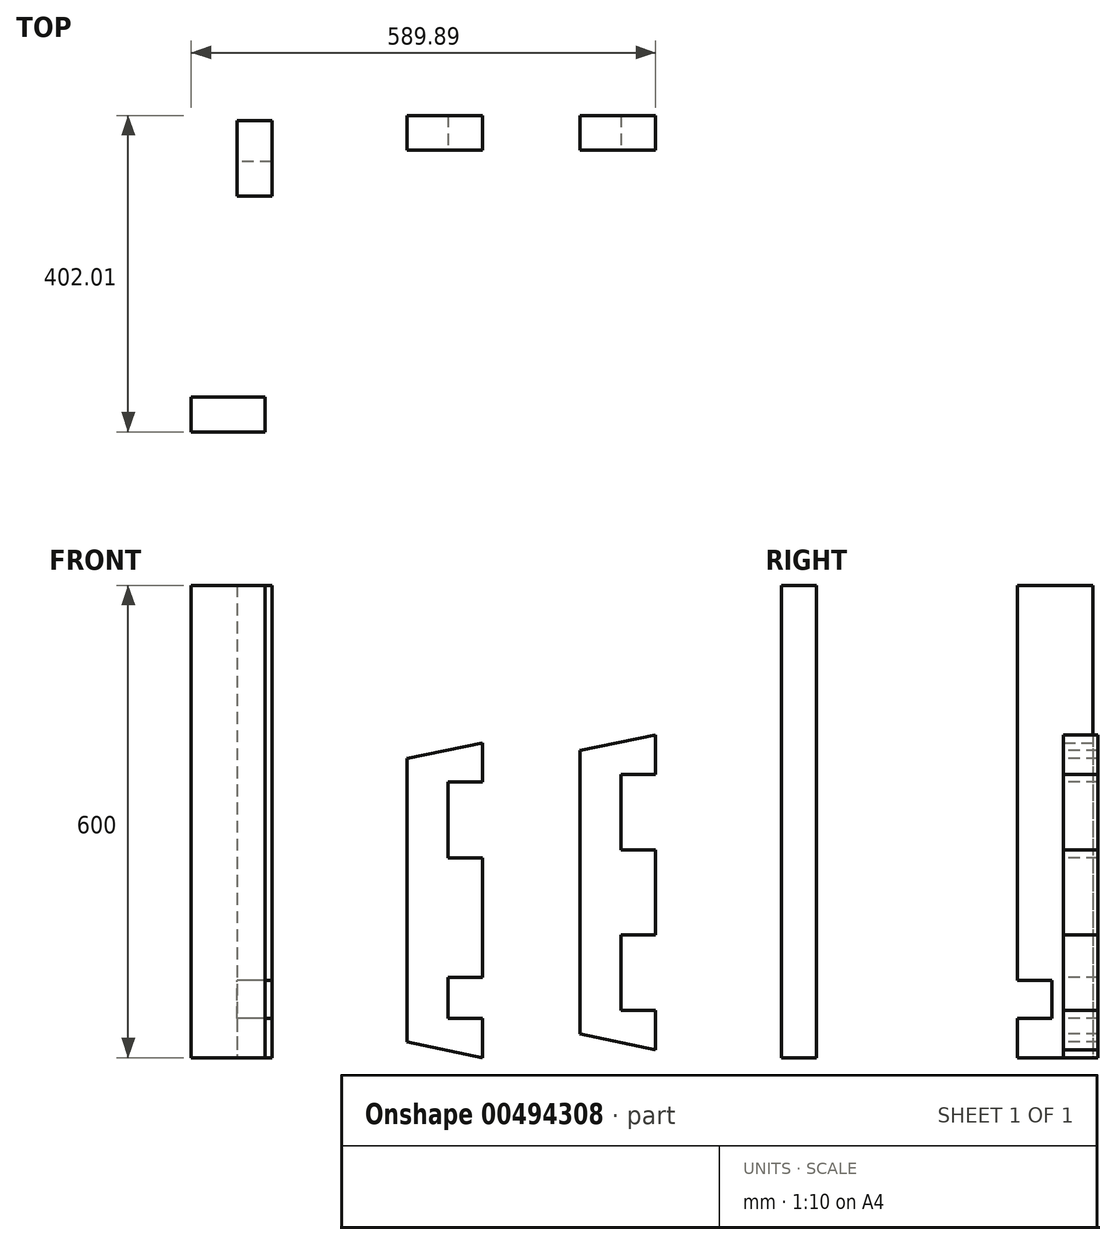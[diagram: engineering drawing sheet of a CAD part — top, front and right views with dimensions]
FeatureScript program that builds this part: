
annotation { "Feature Type Name" : "Feature", "Feature Type Description" : "" }
export const myFeature = defineFeature(function(context is Context, id is Id, definition is map)
    precondition{}
    {
        {
            var Q0;
            Q0=qCreatedBy(makeId("Top.planeOp"),FACE);
            var sketch = newSketch(context, id + "F0", { "sketchPlane" : qUnion([Q0])});
            skLineSegment(sketch, "E0.bottom", {"start": v(0, 0) * mm, "end": v(-96, 0) * mm});
            skLineSegment(sketch, "E0.top", {"start": v(0, 44) * mm, "end": v(-96, 44) * mm});
            skLineSegment(sketch, "E0.left", {"start": v(0, 0) * mm, "end": v(0, 44) * mm});
            skLineSegment(sketch, "E0.right", {"start": v(-96, 0) * mm, "end": v(-96, 44) * mm});
            skSolve(sketch);
        }
        {
            var Q0;
            Q0 = qSketchRegion(id + "F0", true);
            extrude(context, id + "F1", {"entities" : qUnion([Q0]), "depth" : 400 * mm, "offsetDistance" : 25 * mm});
        }
        {
            var Q0;
            Q0=makeQuery(id+"F1.opExtrude","SWEPT_FACE",FACE,{"disambiguationData":[OSD([sQuery(id+"F0.wireOp",EDGE,"E0.bottom")])]});
            var sketch = newSketch(context, id + "F2", { "sketchPlane" : qUnion([Q0])});
            skLineSegment(sketch, "E1.bottom", {"start": v(0, 350) * mm, "end": v(-44, 350) * mm});
            skLineSegment(sketch, "E1.top", {"start": v(0, 254) * mm, "end": v(-44, 254) * mm});
            skLineSegment(sketch, "E1.left", {"start": v(0, 350) * mm, "end": v(0, 254) * mm});
            skLineSegment(sketch, "E1.right", {"start": v(-44, 350) * mm, "end": v(-44, 254) * mm});
            skLineSegment(sketch, "E2.bottom", {"start": v(0, 50) * mm, "end": v(-44, 50) * mm});
            skLineSegment(sketch, "E2.top", {"start": v(0, 102) * mm, "end": v(-44, 102) * mm});
            skLineSegment(sketch, "E2.left", {"start": v(0, 50) * mm, "end": v(0, 102) * mm});
            skLineSegment(sketch, "E2.right", {"start": v(-44, 50) * mm, "end": v(-44, 102) * mm});
            skLineSegment(sketch, "E3", {"start": v(0, 400) * mm, "end": v(-96, 380) * mm});
            skLineSegment(sketch, "E4", {"start": v(0, 0) * mm, "end": v(-96, 20) * mm});
            skSolve(sketch);
        }
        {
            var Q0;
            Q0 = qSketchRegion(id + "F2", true);
            var Q1;
            {var subQ0=sQuery(id+"F2.wireOp",EDGE,"E3");Q1=makeQuery(id+"F2.imprint","IMPRINT",FACE,{"disambiguationData":[TD([[makeQuery(id+"F2.imprint","IMPRINT",EDGE,{"derivedFrom":subQ0}),-1.0]])]});}
            var Q2;
            {var subQ0=sQuery(id+"F2.wireOp",EDGE,"E4");Q2=makeQuery(id+"F2.imprint","IMPRINT",FACE,{"disambiguationData":[TD([[makeQuery(id+"F2.imprint","IMPRINT",EDGE,{"derivedFrom":subQ0}),1.0]])]});}
            extrude(context, id + "F3", {"entities" : qUnion([Q0, Q1, Q2]), "operationType" : NewBodyOperationType.REMOVE, "oppositeDirection" : true, "depth" : 44 * mm, "offsetDistance" : 25 * mm});
        }
        {
            var Q0;
            Q0=qCreatedBy(makeId("Top.planeOp"),FACE);
            var sketch = newSketch(context, id + "F4", { "sketchPlane" : qUnion([Q0])});
            skLineSegment(sketch, "E5.bottom", {"start": v(-311.5, -58.64) * mm, "end": v(-267.5, -58.64) * mm});
            skLineSegment(sketch, "E5.top", {"start": v(-311.5, 37.36) * mm, "end": v(-267.5, 37.36) * mm});
            skLineSegment(sketch, "E5.left", {"start": v(-311.5, -58.64) * mm, "end": v(-311.5, 37.36) * mm});
            skLineSegment(sketch, "E5.right", {"start": v(-267.5, -58.64) * mm, "end": v(-267.5, 37.36) * mm});
            skSolve(sketch);
        }
        {
            var Q0;
            Q0 = qSketchRegion(id + "F4", true);
            extrude(context, id + "F5", {"entities" : qUnion([Q0]), "depth" : 600 * mm, "offsetDistance" : 25 * mm});
        }
        {
            var Q0;
            Q0=makeQuery(id+"F5.opExtrude","SWEPT_FACE",FACE,{"disambiguationData":[OSD([sQuery(id+"F4.wireOp",EDGE,"E5.left")])]});
            var sketch = newSketch(context, id + "F6", { "sketchPlane" : qUnion([Q0])});
            skLineSegment(sketch, "E6.bottom", {"start": v(58.64, 50) * mm, "end": v(14.64, 50) * mm});
            skLineSegment(sketch, "E6.top", {"start": v(58.64, 98) * mm, "end": v(14.64, 98) * mm});
            skLineSegment(sketch, "E6.left", {"start": v(58.64, 50) * mm, "end": v(58.64, 98) * mm});
            skLineSegment(sketch, "E6.right", {"start": v(14.64, 50) * mm, "end": v(14.64, 98) * mm});
            skSolve(sketch);
        }
        {
            var Q0;
            Q0 = qSketchRegion(id + "F6", true);
            extrude(context, id + "F7", {"entities" : qUnion([Q0]), "operationType" : NewBodyOperationType.REMOVE, "oppositeDirection" : true, "depth" : 44 * mm, "offsetDistance" : 25 * mm});
        }
        {
            var Q0;
            Q0=qCreatedBy(makeId("Top.planeOp"),FACE);
            var sketch = newSketch(context, id + "F8", { "sketchPlane" : qUnion([Q0])});
            skLineSegment(sketch, "E7.bottom", {"start": v(-369.89, -358) * mm, "end": v(-275.89, -358) * mm});
            skLineSegment(sketch, "E7.top", {"start": v(-369.89, -314) * mm, "end": v(-275.89, -314) * mm});
            skLineSegment(sketch, "E7.left", {"start": v(-369.89, -358) * mm, "end": v(-369.89, -314) * mm});
            skLineSegment(sketch, "E7.right", {"start": v(-275.89, -358) * mm, "end": v(-275.89, -314) * mm});
            skSolve(sketch);
        }
        {
            var Q0;
            Q0 = qSketchRegion(id + "F8", true);
            extrude(context, id + "F9", {"entities" : qUnion([Q0]), "depth" : 600 * mm, "offsetDistance" : 25 * mm});
        }
        {
            var Q0;
            Q0=makeQuery(id+"F1.opExtrude","SWEPT_BODY",BODY,{"disambiguationData":[OSD([sQuery(id+"F0.wireOp",EDGE,"E0.bottom"),sQuery(id+"F0.wireOp",EDGE,"E0.top"),sQuery(id+"F0.wireOp",EDGE,"E0.left"),sQuery(id+"F0.wireOp",EDGE,"E0.right")])]});
            transform(context, id + "F10", {"entities" : qUnion([Q0]), "transformType" : TransformType.TRANSLATION_3D, "dx" : 220 * mm, "dy" : 0 * mm, "dz" : 10 * mm, "makeCopy" : true});
        }
        {
            var Q0;
            Q0=makeQuery(id+"F10.opPattern","COPY",FACE,{"derivedFrom":makeQuery(id+"F3.boolean.opBoolean","COPY",FACE,{"derivedFrom":makeQuery(id+"F3.opExtrude","SWEPT_FACE",FACE,{"disambiguationData":[OSD([sQuery(id+"F2.wireOp",EDGE,"E2.top")])]})}),"instanceName":"1"});
            extrude(context, id + "F11", {"entities" : qUnion([Q0]), "operationType" : NewBodyOperationType.REMOVE, "oppositeDirection" : true, "depth" : 44 * mm, "offsetDistance" : 25 * mm});
        }
    });
